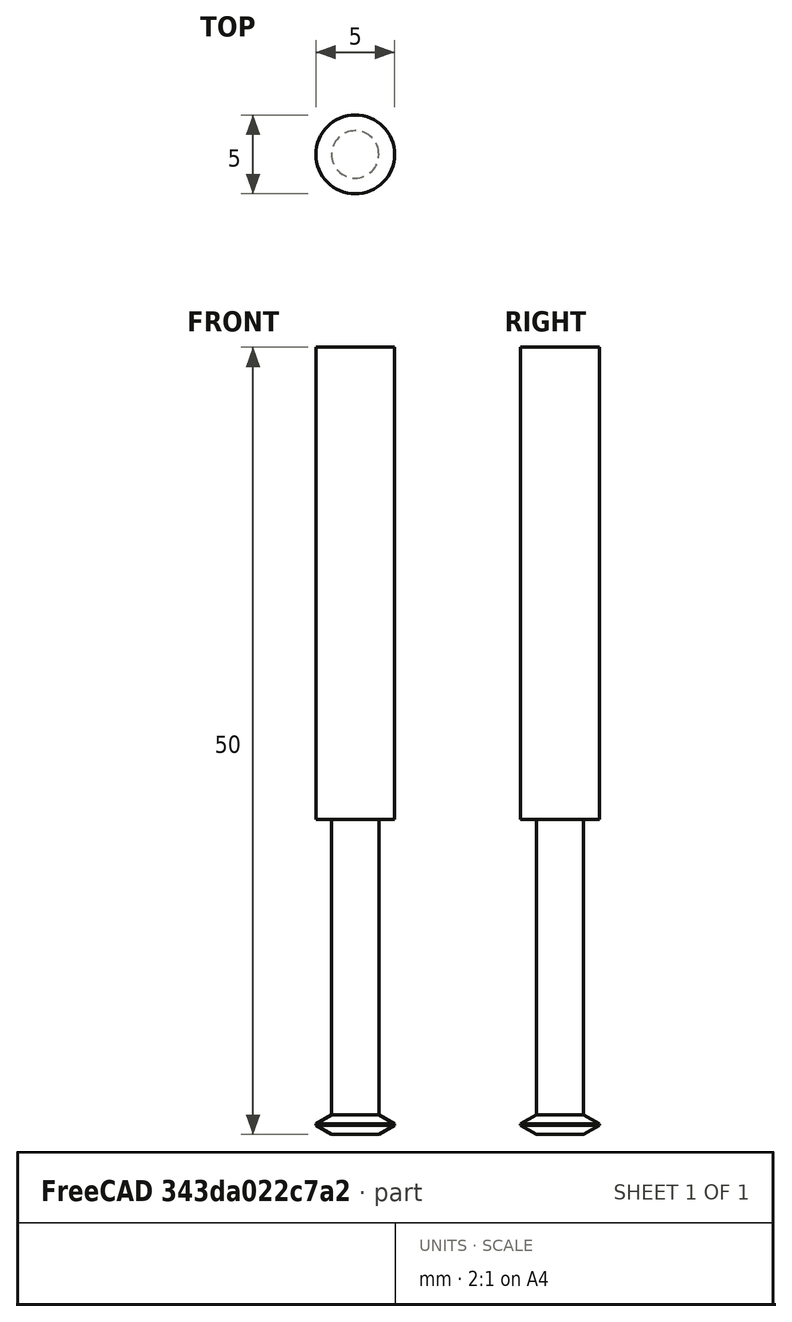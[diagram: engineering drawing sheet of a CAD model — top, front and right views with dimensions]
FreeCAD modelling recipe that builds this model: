
FCSTD DOCUMENT  (FreeCAD 0.21R32460 (Git))
Label: thread-mill
License: Creative Commons Attribution 4.0
LicenseURL: https://creativecommons.org/licenses/by/4.0/
objects: Sketcher::SketchObject×1, PartDesign::Revolution×1, App::FeaturePython×1, PartDesign::Body×1
note: 4 computed .brp shape members not serialized (recipe doc carries the construction recipe); baked Part::Feature solids carry a one-line shape summary decoded from their .brp

FEATURE [Sketcher::SketchObject] Sketch
  FullyConstrained = true
  MapMode = 5
  Placement = pos=(0,0,0) rot=(1,0,0;1.5708rad)
  Support = -> [XZ_Plane]
  expr: Constraints[15] = <<Attributes>>.cuttingAngle
  expr: Constraints[18] = <<Attributes>>.Diameter
  expr: Constraints[19] = <<Attributes>>.cuttingAngle
  expr: Constraints[21] = <<Attributes>>.Crest
  expr: Constraints[27] = <<Attributes>>.NeckLength
  expr: Constraints[30] = <<Attributes>>.NeckDiameter
  expr: Constraints[5] = <<Attributes>>.Length
  expr: Constraints[8] = <<Attributes>>.ShankDiameter
  sketch-geometry (12):
    g0: LineSegment StartX=0 StartY=50 StartZ=0 EndX=0 EndY=0 EndZ=0
    g1: LineSegment StartX=0 StartY=0 StartZ=0 EndX=1.5 EndY=0 EndZ=0
    g2: LineSegment StartX=2.5 StartY=50 StartZ=0 EndX=0 EndY=50 EndZ=0
    g3: LineSegment StartX=1.5 StartY=1.2547 StartZ=0 EndX=2.5 EndY=0.67735 EndZ=0
    g4: LineSegment StartX=1.5 StartY=20 StartZ=0 EndX=1.5 EndY=1.2547 EndZ=0
    g5: LineSegment StartX=-2.5 StartY=50 StartZ=0 EndX=2.5 EndY=50 EndZ=0
    g6: LineSegment StartX=2.5 StartY=0.67735 StartZ=0 EndX=2.5 EndY=0.57735 EndZ=0
    g7: LineSegment StartX=2.5 StartY=0.57735 StartZ=0 EndX=1.5 EndY=0 EndZ=0
    g8: LineSegment StartX=2.5 StartY=0.57735 StartZ=0 EndX=-2.5 EndY=0.57735 EndZ=0
    g9: LineSegment StartX=2.5 StartY=50 StartZ=0 EndX=2.5 EndY=20.01 EndZ=0
    g10: LineSegment StartX=2.5 StartY=20.01 StartZ=0 EndX=1.5 EndY=20 EndZ=0
    g11: LineSegment StartX=1.5 StartY=20 StartZ=0 EndX=-1.5 EndY=20 EndZ=0
  constraints (32):
    c: Vertical(g0)
    c: Coincident(g0,g1)
    c: Horizontal(g1)
    c: Horizontal(g2)
    c: Coincident(g0,g2)
    c: DistanceY(g1,g2) = 50
    c: Vertical(g4)
    c: Symmetric(g5,g5,g0)
    c: DistanceX(g5,g5) = 5
    c: Coincident(g3,g4)
    c: Coincident(g0,g-1)
    c: Coincident(g6,g3)
    c: Vertical(g6)
    c: Coincident(g7,g6)
    c: Coincident(g7,g1)
    c: Angle(g3,g7) = 1.0472
    c: Coincident(g8,g6)
    c: Symmetric(g6,g8,g-2)
    c: DistanceX(g8,g8) = 5
    c: Angle(g-2,g3) = 1.0472
    c: Vertical(g1,g3)
    c: DistanceY(g6,g6) = 0.1
    c: Coincident(g5,g2)
    c: Coincident(g2,g9)
    c: Vertical(g9)
    c: Coincident(g9,g10)
    c: Coincident(g10,g4)
    c: DistanceY(g4) = 20
    c: Coincident(g11,g4)
    c: Symmetric(g4,g11,g0)
    c: DistanceX(g11,g11) = 3
    c: DistanceY(g4,g9) = 0.01
FEATURE [PartDesign::Revolution] Revolution
  AllowMultiFace = false
  Angle = 360
  Axis = (0,-2e-16,1)
  Base = (0,0,0)
  Placement = pos=(0,0,0) rot=(1,0,0;1.5708rad)
  Profile = -> Sketch
  ReferenceAxis = -> Sketch [V_Axis]
  Reversed = true
FEATURE [App::FeaturePython] PropertyBag  label="Attributes"  # WARN: FeaturePython — macro-defined, semantics opaque (R4)
  Chipload = 0
  Crest = 0.1
  CustomPropertyGroups = Attributes | Shape
  Diameter = 5
  Flutes = 0
  Length = 50
  Material = 0
  NeckDiameter = 3
  NeckLength = 20
  ShankDiameter = 5
  cuttingAngle = 60
FEATURE [PartDesign::Body] Body  label="ThreadMill"
  Group = -> [Sketch,Revolution,PropertyBag]
  Origin = -> Origin
  Tip = -> Revolution
